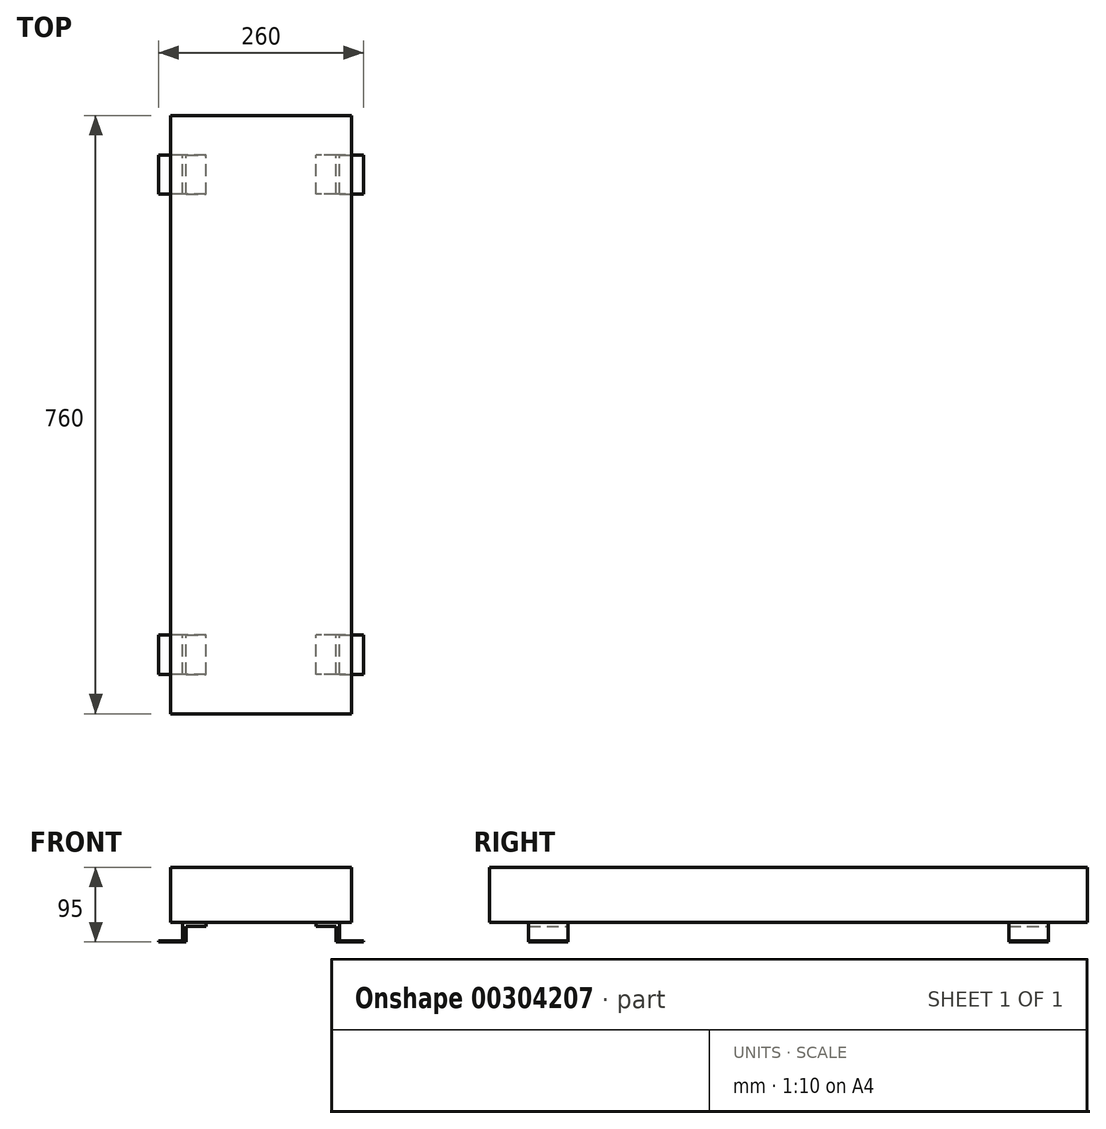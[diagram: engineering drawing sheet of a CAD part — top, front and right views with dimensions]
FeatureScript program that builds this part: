
annotation { "Feature Type Name" : "Feature", "Feature Type Description" : "" }
export const myFeature = defineFeature(function(context is Context, id is Id, definition is map)
    precondition{}
    {
        {
            var Q0;
            Q0=qCreatedBy(makeId("Front.planeOp"),FACE);
            var sketch = newSketch(context, id + "F0", { "sketchPlane" : qUnion([Q0])});
            skLineSegment(sketch, "E0.bottom", {"start": v(-115, 70) * mm, "end": v(115, 70) * mm});
            skLineSegment(sketch, "E0.top", {"start": v(-115, 0) * mm, "end": v(115, 0) * mm});
            skLineSegment(sketch, "E0.left", {"start": v(-115, 70) * mm, "end": v(-115, 0) * mm});
            skLineSegment(sketch, "E0.right", {"start": v(115, 70) * mm, "end": v(115, 0) * mm});
            skLineSegment(sketch, "E1", {"start": v(70, 0) * mm, "end": v(70, -5) * mm});
            skLineSegment(sketch, "E2", {"start": v(70, -5) * mm, "end": v(95, -5) * mm});
            skLineSegment(sketch, "E3", {"start": v(95, -5) * mm, "end": v(95, -25) * mm});
            skLineSegment(sketch, "E4", {"start": v(95, -25) * mm, "end": v(130, -25) * mm});
            skLineSegment(sketch, "E5", {"start": v(130, -25) * mm, "end": v(130, -23.5) * mm});
            skLineSegment(sketch, "E6", {"start": v(130, -23.5) * mm, "end": v(100, -23.5) * mm});
            skLineSegment(sketch, "E7", {"start": v(100, -23.5) * mm, "end": v(100, 0) * mm});
            skLineSegment(sketch, "E8.MirrorCS", {"start": v(-70, 0) * mm, "end": v(-70, -5) * mm});
            skLineSegment(sketch, "E9.MirrorCS", {"start": v(-70, -5) * mm, "end": v(-95, -5) * mm});
            skLineSegment(sketch, "E10.MirrorCS", {"start": v(-95, -5) * mm, "end": v(-95, -25) * mm});
            skLineSegment(sketch, "E11.MirrorCS", {"start": v(-95, -25) * mm, "end": v(-130, -25) * mm});
            skLineSegment(sketch, "E12.MirrorCS", {"start": v(-130, -25) * mm, "end": v(-130, -23.5) * mm});
            skLineSegment(sketch, "E13.MirrorCS", {"start": v(-130, -23.5) * mm, "end": v(-100, -23.5) * mm});
            skLineSegment(sketch, "E14.MirrorCS", {"start": v(-100, -23.5) * mm, "end": v(-100, 0) * mm});
            skSolve(sketch);
        }
        {
            var Q0;
            Q0 = qSketchRegion(id + "F0", true);
            extrude(context, id + "F1", {"entities" : qUnion([Q0]), "depth" : 760 * mm});
        }
        {
            var Q0;
            Q0=makeQuery(id+"F1.opExtrude","SWEPT_FACE",FACE,{"disambiguationData":[OSD([sQuery(id+"F0.wireOp",EDGE,"E12.MirrorCS")])]});
            var sketch = newSketch(context, id + "F2", { "sketchPlane" : qUnion([Q0])});
            skLineSegment(sketch, "E15.bottom", {"start": v(0, 0) * mm, "end": v(50, 0) * mm});
            skLineSegment(sketch, "E15.top", {"start": v(0, -25) * mm, "end": v(50, -25) * mm});
            skLineSegment(sketch, "E15.left", {"start": v(0, 0) * mm, "end": v(0, -25) * mm});
            skLineSegment(sketch, "E15.right", {"start": v(50, 0) * mm, "end": v(50, -25) * mm});
            skLineSegment(sketch, "E16.bottom", {"start": v(760, 0) * mm, "end": v(710, 0) * mm});
            skLineSegment(sketch, "E16.top", {"start": v(760, -25) * mm, "end": v(710, -25) * mm});
            skLineSegment(sketch, "E16.left", {"start": v(760, 0) * mm, "end": v(760, -25) * mm});
            skLineSegment(sketch, "E16.right", {"start": v(710, 0) * mm, "end": v(710, -25) * mm});
            skLineSegment(sketch, "E17.bottom", {"start": v(100, 0) * mm, "end": v(660, 0) * mm});
            skLineSegment(sketch, "E17.top", {"start": v(100, -25) * mm, "end": v(660, -25) * mm});
            skLineSegment(sketch, "E17.left", {"start": v(100, 0) * mm, "end": v(100, -25) * mm});
            skLineSegment(sketch, "E17.right", {"start": v(660, 0) * mm, "end": v(660, -25) * mm});
            skSolve(sketch);
        }
        {
            var Q0;
            Q0 = qSketchRegion(id + "F2", true);
            extrude(context, id + "F3", {"entities" : qUnion([Q0]), "operationType" : NewBodyOperationType.REMOVE, "endBound" : BoundingType.THROUGH_ALL, "oppositeDirection" : true, "depth" : 25 * mm});
        }
    });
